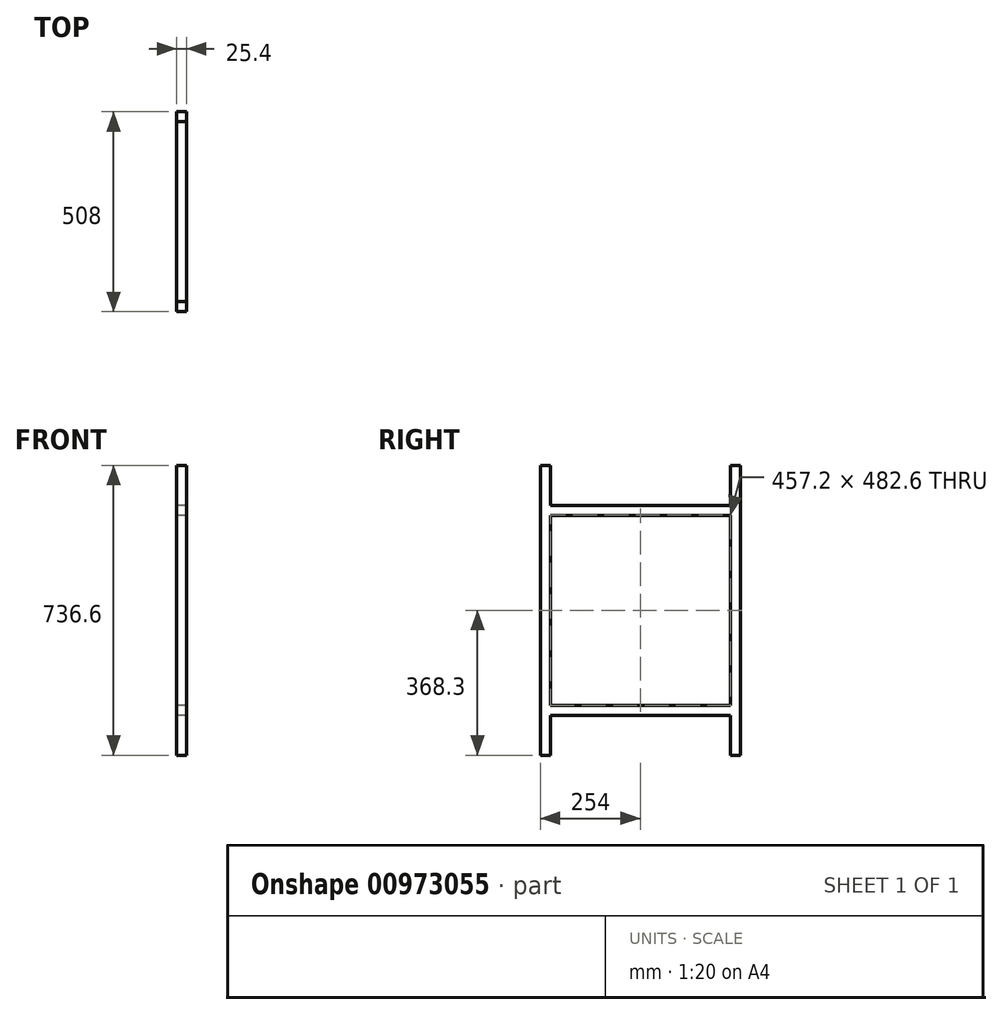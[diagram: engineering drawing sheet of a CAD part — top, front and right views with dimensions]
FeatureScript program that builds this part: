
annotation { "Feature Type Name" : "Feature", "Feature Type Description" : "" }
export const myFeature = defineFeature(function(context is Context, id is Id, definition is map)
    precondition{}
    {
        {
            var Q0;
            Q0=qCreatedBy(makeId("Right.planeOp"),FACE);
            var sketch = newSketch(context, id + "F0", { "sketchPlane" : qUnion([Q0])});
            skLineSegment(sketch, "E0.bottom", {"start": v(0, 0) * mm, "end": v(25.4, 0) * mm});
            skLineSegment(sketch, "E0.top", {"start": v(0, 736.6) * mm, "end": v(25.4, 736.6) * mm});
            skLineSegment(sketch, "E0.left", {"start": v(0, 0) * mm, "end": v(0, 736.6) * mm});
            skLineSegment(sketch, "E0.right", {"start": v(25.4, 0) * mm, "end": v(25.4, 101.6) * mm});
            skLineSegment(sketch, "E1.bottom", {"start": v(25.4, 127) * mm, "end": v(482.6, 127) * mm});
            skLineSegment(sketch, "E1.top", {"start": v(25.4, 101.6) * mm, "end": v(482.6, 101.6) * mm});
            skLineSegment(sketch, "E2.bottom", {"start": v(482.6, 736.6) * mm, "end": v(508, 736.6) * mm});
            skLineSegment(sketch, "E2.top", {"start": v(482.6, 0) * mm, "end": v(508, 0) * mm});
            skLineSegment(sketch, "E2.left", {"start": v(482.6, 736.6) * mm, "end": v(482.6, 635) * mm});
            skLineSegment(sketch, "E2.right", {"start": v(508, 736.6) * mm, "end": v(508, 0) * mm});
            skLineSegment(sketch, "E3.bottom", {"start": v(25.4, 635) * mm, "end": v(482.6, 635) * mm});
            skLineSegment(sketch, "E3.top", {"start": v(25.4, 609.6) * mm, "end": v(482.6, 609.6) * mm});
            skLineSegment(sketch, "E4.trimOffspring", {"start": v(25.4, 635) * mm, "end": v(25.4, 736.6) * mm});
            skLineSegment(sketch, "E5.trimOffspring", {"start": v(482.6, 609.6) * mm, "end": v(482.6, 127) * mm});
            skLineSegment(sketch, "E6.trimOffspring", {"start": v(482.6, 101.6) * mm, "end": v(482.6, 0) * mm});
            skLineSegment(sketch, "E7.trimOffspring", {"start": v(25.4, 127) * mm, "end": v(25.4, 609.6) * mm});
            skSolve(sketch);
        }
        {
            var Q0;
            Q0=makeQuery(id+"F0.imprint","IMPRINT",FACE,{"disambiguationData":[TD([[makeQuery(id+"F0.imprint","IMPRINT",EDGE,{"derivedFrom":sQuery(id+"F0.wireOp",EDGE,"E0.bottom")}),1.0]])]});
            extrude(context, id + "F1", {"entities" : qUnion([Q0]), "depth" : 25.4 * mm, "offsetDistance" : 25.4 * mm});
        }
    });
